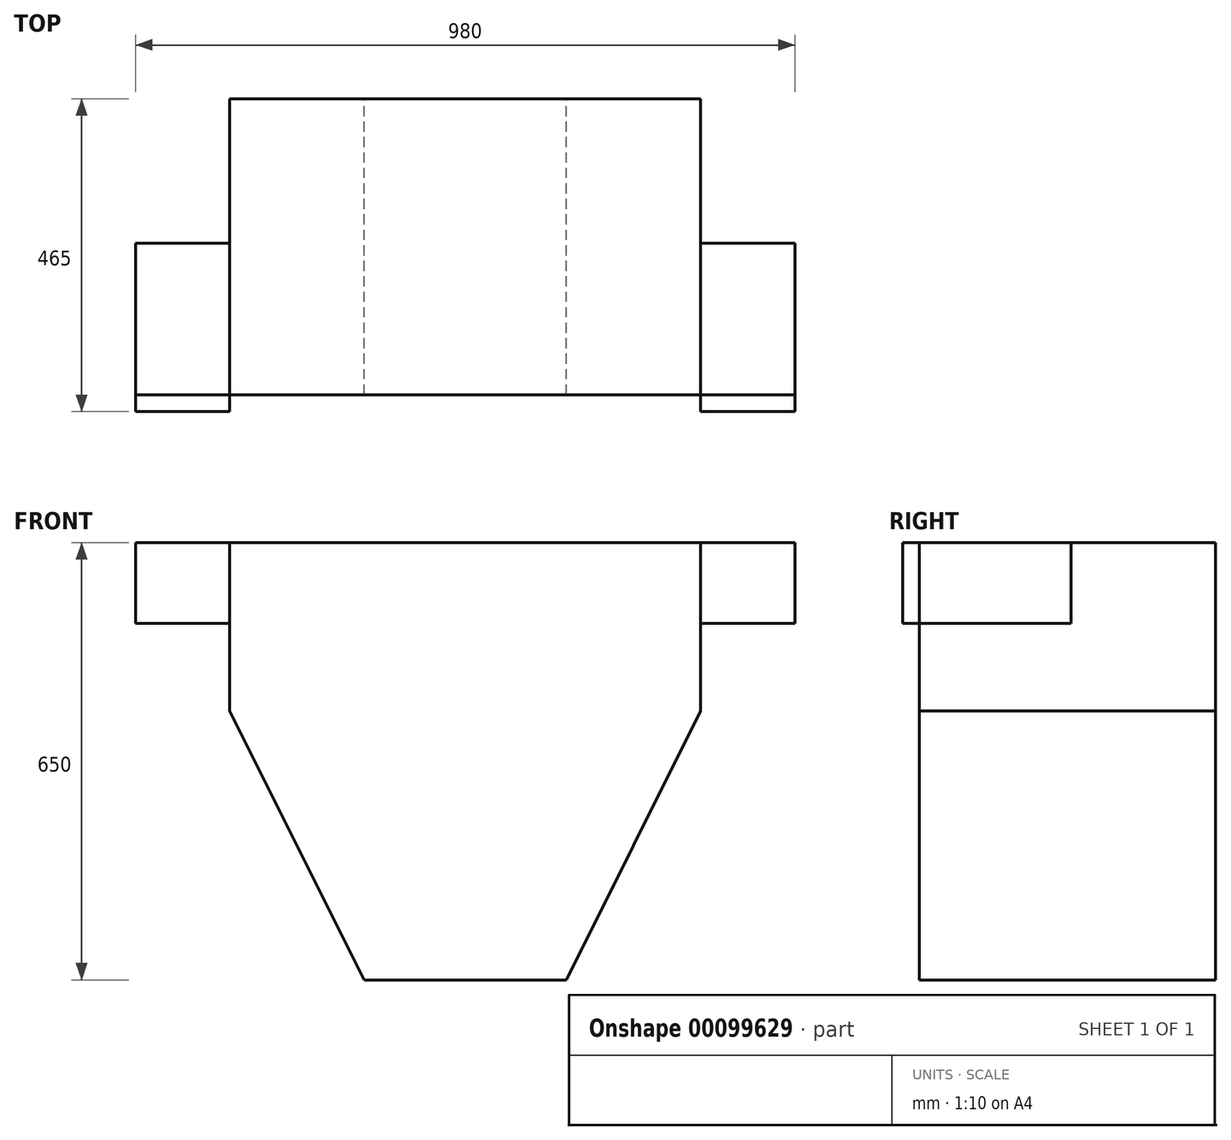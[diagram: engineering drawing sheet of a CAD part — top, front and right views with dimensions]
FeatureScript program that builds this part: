
annotation { "Feature Type Name" : "Feature", "Feature Type Description" : "" }
export const myFeature = defineFeature(function(context is Context, id is Id, definition is map)
    precondition{}
    {
        {
            var Q0;
            Q0=qCreatedBy(makeId("Front.planeOp"),FACE);
            var sketch = newSketch(context, id + "F0", { "sketchPlane" : qUnion([Q0])});
            skLineSegment(sketch, "E0.bottom", {"start": v(150, -325) * mm, "end": v(-150, -325) * mm});
            skLineSegment(sketch, "E0.top", {"start": v(350, 325) * mm, "end": v(-350, 325) * mm});
            skLineSegment(sketch, "E0.left", {"start": v(350, 75) * mm, "end": v(350, 325) * mm});
            skLineSegment(sketch, "E0.right", {"start": v(-350, 75) * mm, "end": v(-350, 325) * mm});
            skPoint(sketch, "E0.middle", {"position": v(0, 0) * mm});
            skLineSegment(sketch, "E1", {"start": v(-350, 75) * mm, "end": v(-150, -325) * mm});
            skLineSegment(sketch, "E2", {"start": v(350, 75) * mm, "end": v(150, -325) * mm});
            skPoint(sketch, "E3.orphan", {"position": v(-350, -325) * mm});
            skPoint(sketch, "E4.orphan", {"position": v(350, -325) * mm});
            skSolve(sketch);
        }
        {
            var Q0;
            Q0 = qSketchRegion(id + "F0", true);
            extrude(context, id + "F1", {"entities" : qUnion([Q0]), "depth" : 440 * mm});
        }
        {
            var Q0;
            Q0=makeQuery(id+"F1.opExtrude","CAP_FACE",FACE,{"disambiguationData":[OSD([sQuery(id+"F0.wireOp",EDGE,"E0.bottom"),sQuery(id+"F0.wireOp",EDGE,"E0.top"),sQuery(id+"F0.wireOp",EDGE,"E0.left"),sQuery(id+"F0.wireOp",EDGE,"E0.right"),sQuery(id+"F0.wireOp",EDGE,"E1"),sQuery(id+"F0.wireOp",EDGE,"E2")])],"isStart":false});
            var sketch = newSketch(context, id + "F2", { "sketchPlane" : qUnion([Q0])});
            skLineSegment(sketch, "E5.bottom", {"start": v(-350, 325) * mm, "end": v(-490, 325) * mm});
            skLineSegment(sketch, "E5.top", {"start": v(-350, 205) * mm, "end": v(-490, 205) * mm});
            skLineSegment(sketch, "E5.left", {"start": v(-350, 325) * mm, "end": v(-350, 205) * mm});
            skLineSegment(sketch, "E5.right", {"start": v(-490, 325) * mm, "end": v(-490, 205) * mm});
            skLineSegment(sketch, "E6.bottom", {"start": v(350, 325) * mm, "end": v(490, 325) * mm});
            skLineSegment(sketch, "E6.top", {"start": v(350, 205) * mm, "end": v(490, 205) * mm});
            skLineSegment(sketch, "E6.left", {"start": v(350, 325) * mm, "end": v(350, 205) * mm});
            skLineSegment(sketch, "E6.right", {"start": v(490, 325) * mm, "end": v(490, 205) * mm});
            skSolve(sketch);
        }
        {
            var Q0;
            Q0 = qSketchRegion(id + "F2", true);
            extrude(context, id + "F3", {"entities" : qUnion([Q0]), "depth" : 25 * mm});
        }
        {
            var Q0;
            Q0=makeQuery(id+"F3.opExtrude","CAP_FACE",FACE,{"disambiguationData":[OSD([sQuery(id+"F2.wireOp",EDGE,"E5.bottom"),sQuery(id+"F2.wireOp",EDGE,"E5.top"),sQuery(id+"F2.wireOp",EDGE,"E5.left"),sQuery(id+"F2.wireOp",EDGE,"E5.right")])],"isStart":false});
            var Q1;
            Q1=makeQuery(id+"F3.opExtrude","CAP_FACE",FACE,{"disambiguationData":[OSD([sQuery(id+"F2.wireOp",EDGE,"E6.bottom"),sQuery(id+"F2.wireOp",EDGE,"E6.top"),sQuery(id+"F2.wireOp",EDGE,"E6.left"),sQuery(id+"F2.wireOp",EDGE,"E6.right")])],"isStart":false});
            extrude(context, id + "F4", {"entities" : qUnion([Q0, Q1]), "oppositeDirection" : true, "depth" : 250 * mm});
        }
    });
